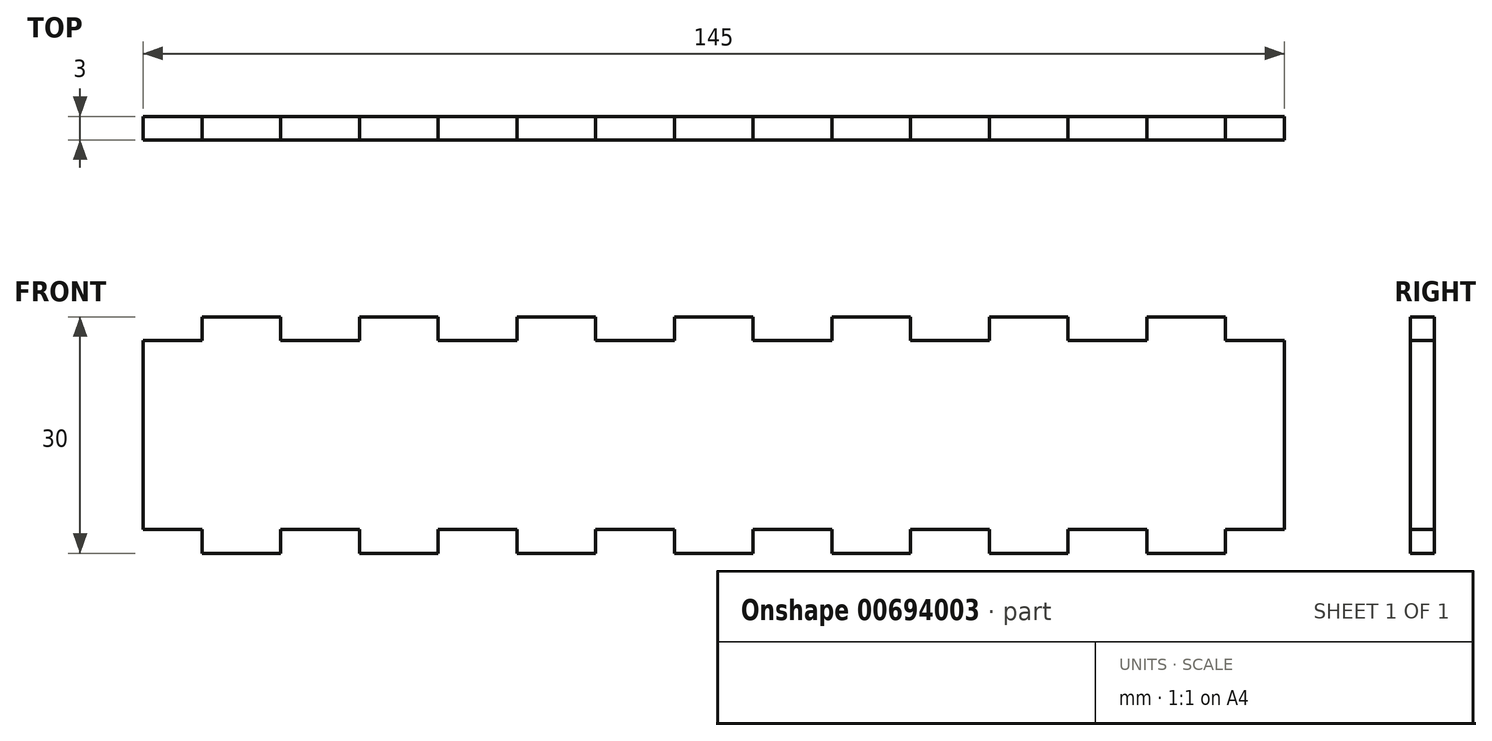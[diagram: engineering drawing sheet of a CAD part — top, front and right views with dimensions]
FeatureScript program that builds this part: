
annotation { "Feature Type Name" : "Feature", "Feature Type Description" : "" }
export const myFeature = defineFeature(function(context is Context, id is Id, definition is map)
    precondition{}
    {
        {
            var Q0;
            Q0=qCreatedBy(makeId("Front.planeOp"),FACE);
            var sketch = newSketch(context, id + "F0", { "sketchPlane" : qUnion([Q0])});
            skLineSegment(sketch, "E0.bottom", {"start": v(72.5, 15) * mm, "end": v(-72.5, 15) * mm});
            skLineSegment(sketch, "E0.top", {"start": v(72.5, -15) * mm, "end": v(-72.5, -15) * mm});
            skLineSegment(sketch, "E0.left", {"start": v(72.5, 15) * mm, "end": v(72.5, -15) * mm});
            skLineSegment(sketch, "E0.right", {"start": v(-72.5, 15) * mm, "end": v(-72.5, -15) * mm});
            skPoint(sketch, "E0.middle", {"position": v(0, 0) * mm});
            skSolve(sketch);
        }
        {
            var Q0;
            Q0=makeQuery(id+"F0.imprint","IMPRINT",FACE,{"disambiguationData":[TD([[makeQuery(id+"F0.imprint","IMPRINT",EDGE,{"derivedFrom":sQuery(id+"F0.wireOp",EDGE,"E0.bottom")}),1.0]])]});
            extrude(context, id + "F1", {"entities" : qUnion([Q0]), "depth" : 3 * mm, "offsetDistance" : 25 * mm});
        }
        {
            var Q0;
            Q0=makeQuery(id+"F1.opExtrude","CAP_FACE",FACE,{"disambiguationData":[OSD([sQuery(id+"F0.wireOp",EDGE,"E0.bottom"),sQuery(id+"F0.wireOp",EDGE,"E0.top"),sQuery(id+"F0.wireOp",EDGE,"E0.left"),sQuery(id+"F0.wireOp",EDGE,"E0.right")])],"isStart":false});
            var sketch = newSketch(context, id + "F2", { "sketchPlane" : qUnion([Q0])});
            skLineSegment(sketch, "E1", {"start": v(-75, -15) * mm, "end": v(-72.5, -15) * mm, "construction": true});
            skLineSegment(sketch, "E2.bottom", {"start": v(-75, -15) * mm, "end": v(-65, -15) * mm});
            skLineSegment(sketch, "E2.top", {"start": v(-75, -12) * mm, "end": v(-65, -12) * mm});
            skLineSegment(sketch, "E2.left", {"start": v(-75, -15) * mm, "end": v(-75, -12) * mm});
            skLineSegment(sketch, "E2.right", {"start": v(-65, -15) * mm, "end": v(-65, -12) * mm});
            skLineSegment(sketch, "E3.0.1.0", {"start": v(-75, 15) * mm, "end": v(-65, 15) * mm});
            skLineSegment(sketch, "E3.0.1.1", {"start": v(-75, 12) * mm, "end": v(-65, 12) * mm});
            skLineSegment(sketch, "E3.0.1.2", {"start": v(-65, 12) * mm, "end": v(-65, 15) * mm});
            skLineSegment(sketch, "E3.0.1.3", {"start": v(-75, 12) * mm, "end": v(-75, 15) * mm});
            skLineSegment(sketch, "E3.1.0.0", {"start": v(-55, -12) * mm, "end": v(-45, -12) * mm});
            skLineSegment(sketch, "E3.1.0.1", {"start": v(-55, -15) * mm, "end": v(-45, -15) * mm});
            skLineSegment(sketch, "E3.1.0.2", {"start": v(-45, -15) * mm, "end": v(-45, -12) * mm});
            skLineSegment(sketch, "E3.1.0.3", {"start": v(-55, -15) * mm, "end": v(-55, -12) * mm});
            skLineSegment(sketch, "E3.1.1.0", {"start": v(-55, 15) * mm, "end": v(-45, 15) * mm});
            skLineSegment(sketch, "E3.1.1.1", {"start": v(-55, 12) * mm, "end": v(-45, 12) * mm});
            skLineSegment(sketch, "E3.1.1.2", {"start": v(-45, 12) * mm, "end": v(-45, 15) * mm});
            skLineSegment(sketch, "E3.1.1.3", {"start": v(-55, 12) * mm, "end": v(-55, 15) * mm});
            skLineSegment(sketch, "E3.2.0.0", {"start": v(-35, -12) * mm, "end": v(-25, -12) * mm});
            skLineSegment(sketch, "E3.2.0.1", {"start": v(-35, -15) * mm, "end": v(-25, -15) * mm});
            skLineSegment(sketch, "E3.2.0.2", {"start": v(-25, -15) * mm, "end": v(-25, -12) * mm});
            skLineSegment(sketch, "E3.2.0.3", {"start": v(-35, -15) * mm, "end": v(-35, -12) * mm});
            skLineSegment(sketch, "E3.2.1.0", {"start": v(-35, 15) * mm, "end": v(-25, 15) * mm});
            skLineSegment(sketch, "E3.2.1.1", {"start": v(-35, 12) * mm, "end": v(-25, 12) * mm});
            skLineSegment(sketch, "E3.2.1.2", {"start": v(-25, 12) * mm, "end": v(-25, 15) * mm});
            skLineSegment(sketch, "E3.2.1.3", {"start": v(-35, 12) * mm, "end": v(-35, 15) * mm});
            skLineSegment(sketch, "E3.3.0.0", {"start": v(-15, -12) * mm, "end": v(-5, -12) * mm});
            skLineSegment(sketch, "E3.3.0.1", {"start": v(-15, -15) * mm, "end": v(-5, -15) * mm});
            skLineSegment(sketch, "E3.3.0.2", {"start": v(-5, -15) * mm, "end": v(-5, -12) * mm});
            skLineSegment(sketch, "E3.3.0.3", {"start": v(-15, -15) * mm, "end": v(-15, -12) * mm});
            skLineSegment(sketch, "E3.3.1.0", {"start": v(-15, 15) * mm, "end": v(-5, 15) * mm});
            skLineSegment(sketch, "E3.3.1.1", {"start": v(-15, 12) * mm, "end": v(-5, 12) * mm});
            skLineSegment(sketch, "E3.3.1.2", {"start": v(-5, 12) * mm, "end": v(-5, 15) * mm});
            skLineSegment(sketch, "E3.3.1.3", {"start": v(-15, 12) * mm, "end": v(-15, 15) * mm});
            skLineSegment(sketch, "E3.4.0.0", {"start": v(5, -12) * mm, "end": v(15, -12) * mm});
            skLineSegment(sketch, "E3.4.0.1", {"start": v(5, -15) * mm, "end": v(15, -15) * mm});
            skLineSegment(sketch, "E3.4.0.2", {"start": v(15, -15) * mm, "end": v(15, -12) * mm});
            skLineSegment(sketch, "E3.4.0.3", {"start": v(5, -15) * mm, "end": v(5, -12) * mm});
            skLineSegment(sketch, "E3.4.1.0", {"start": v(5, 15) * mm, "end": v(15, 15) * mm});
            skLineSegment(sketch, "E3.4.1.1", {"start": v(5, 12) * mm, "end": v(15, 12) * mm});
            skLineSegment(sketch, "E3.4.1.2", {"start": v(15, 12) * mm, "end": v(15, 15) * mm});
            skLineSegment(sketch, "E3.4.1.3", {"start": v(5, 12) * mm, "end": v(5, 15) * mm});
            skLineSegment(sketch, "E3.5.0.0", {"start": v(25, -12) * mm, "end": v(35, -12) * mm});
            skLineSegment(sketch, "E3.5.0.1", {"start": v(25, -15) * mm, "end": v(35, -15) * mm});
            skLineSegment(sketch, "E3.5.0.2", {"start": v(35, -15) * mm, "end": v(35, -12) * mm});
            skLineSegment(sketch, "E3.5.0.3", {"start": v(25, -15) * mm, "end": v(25, -12) * mm});
            skLineSegment(sketch, "E3.5.1.0", {"start": v(25, 15) * mm, "end": v(35, 15) * mm});
            skLineSegment(sketch, "E3.5.1.1", {"start": v(25, 12) * mm, "end": v(35, 12) * mm});
            skLineSegment(sketch, "E3.5.1.2", {"start": v(35, 12) * mm, "end": v(35, 15) * mm});
            skLineSegment(sketch, "E3.5.1.3", {"start": v(25, 12) * mm, "end": v(25, 15) * mm});
            skLineSegment(sketch, "E3.6.0.0", {"start": v(45, -12) * mm, "end": v(55, -12) * mm});
            skLineSegment(sketch, "E3.6.0.1", {"start": v(45, -15) * mm, "end": v(55, -15) * mm});
            skLineSegment(sketch, "E3.6.0.2", {"start": v(55, -15) * mm, "end": v(55, -12) * mm});
            skLineSegment(sketch, "E3.6.0.3", {"start": v(45, -15) * mm, "end": v(45, -12) * mm});
            skLineSegment(sketch, "E3.6.1.0", {"start": v(45, 15) * mm, "end": v(55, 15) * mm});
            skLineSegment(sketch, "E3.6.1.1", {"start": v(45, 12) * mm, "end": v(55, 12) * mm});
            skLineSegment(sketch, "E3.6.1.2", {"start": v(55, 12) * mm, "end": v(55, 15) * mm});
            skLineSegment(sketch, "E3.6.1.3", {"start": v(45, 12) * mm, "end": v(45, 15) * mm});
            skLineSegment(sketch, "E3.direction1", {"start": v(-75, -12) * mm, "end": v(-55, -12) * mm, "construction": true});
            skLineSegment(sketch, "E3.direction2", {"start": v(-75, -12) * mm, "end": v(-75, 15) * mm, "construction": true});
            skLineSegment(sketch, "E4.0.7.0", {"start": v(65, -12) * mm, "end": v(75, -12) * mm});
            skLineSegment(sketch, "E4.3.7.0", {"start": v(65, -15) * mm, "end": v(75, -15) * mm});
            skLineSegment(sketch, "E4.6.7.0", {"start": v(75, -15) * mm, "end": v(75, -12) * mm});
            skLineSegment(sketch, "E4.9.7.0", {"start": v(65, -15) * mm, "end": v(65, -12) * mm});
            skLineSegment(sketch, "E4.0.7.1", {"start": v(65, 15) * mm, "end": v(75, 15) * mm});
            skLineSegment(sketch, "E4.3.7.1", {"start": v(65, 12) * mm, "end": v(75, 12) * mm});
            skLineSegment(sketch, "E4.6.7.1", {"start": v(75, 12) * mm, "end": v(75, 15) * mm});
            skLineSegment(sketch, "E4.9.7.1", {"start": v(65, 12) * mm, "end": v(65, 15) * mm});
            skSolve(sketch);
        }
        {
            var Q0;
            Q0 = qSketchRegion(id + "F2", true);
            extrude(context, id + "F3", {"entities" : qUnion([Q0]), "operationType" : NewBodyOperationType.REMOVE, "oppositeDirection" : true, "depth" : 25 * mm, "offsetDistance" : 25 * mm});
        }
    });
